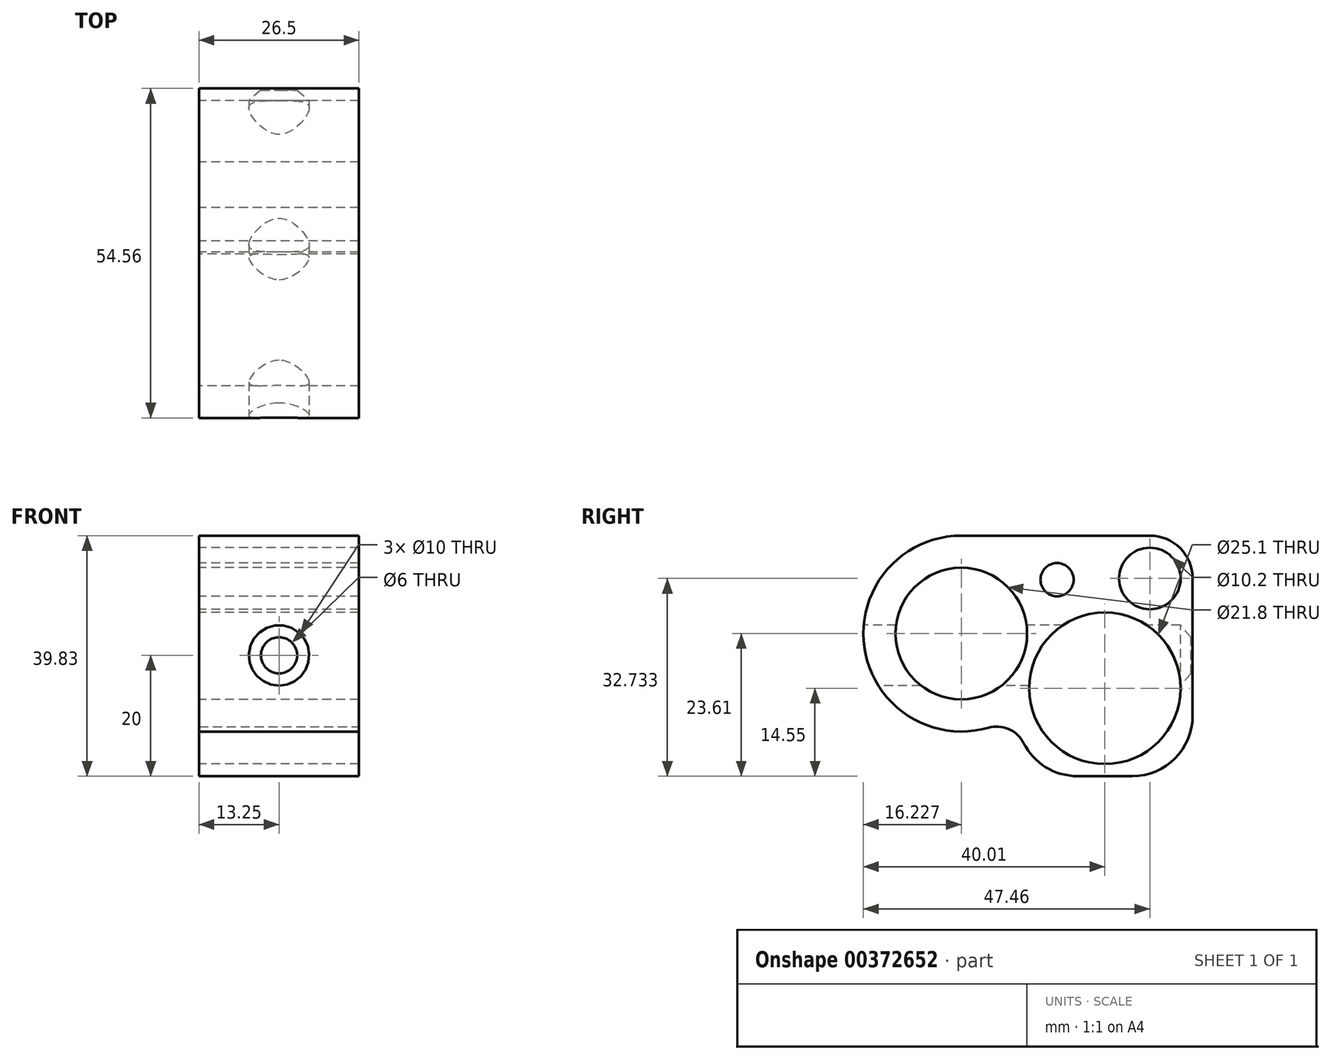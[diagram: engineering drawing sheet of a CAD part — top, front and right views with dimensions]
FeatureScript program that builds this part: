
annotation { "Feature Type Name" : "Feature", "Feature Type Description" : "" }
export const myFeature = defineFeature(function(context is Context, id is Id, definition is map)
    precondition{}
    {
        {
            var Q0;
            Q0=qCreatedBy(makeId("Right.planeOp"),FACE);
            var sketch = newSketch(context, id + "F0", { "sketchPlane" : qUnion([Q0])});
            skCircle(sketch, "E0", {"center": v(0, 0) * mm, "radius": 12.55 * mm});
            skCircle(sketch, "E1", {"center": v(-7.92, 17.98) * mm, "radius": 4.3 * mm, "construction": true});
            skCircle(sketch, "E2", {"center": v(7.45, 18.18) * mm, "radius": 5.1 * mm});
            skLineSegment(sketch, "E3", {"start": v(-7.92, 17.98) * mm, "end": v(0, 0) * mm, "construction": true});
            skLineSegment(sketch, "E4", {"start": v(7.45, 18.18) * mm, "end": v(0, 0) * mm, "construction": true});
            skCircle(sketch, "E5", {"center": v(-23.78, 9.06) * mm, "radius": 10.9 * mm});
            skLineSegment(sketch, "E6", {"start": v(-23.78, 9.06) * mm, "end": v(0, 0) * mm, "construction": true});
            skArc(sketch, "E7", {"start": v(-23.78, 25.28) * mm, "mid": v(-39.27, 4.22) * mm, "end": v(-14.55, -4.28) * mm});
            skArc(sketch, "E8", {"start": v(14.55, 18.18) * mm, "mid": v(12.47, 23.2) * mm, "end": v(7.45, 25.28) * mm});
            skLineSegment(sketch, "E9", {"start": v(7.45, 25.28) * mm, "end": v(-23.78, 25.28) * mm});
            skLineSegment(sketch, "E10", {"start": v(14.55, 18.18) * mm, "end": v(14.55, -14.55) * mm});
            skPoint(sketch, "E10.endSnap0", {"position": v(14.55, 18.18) * mm});
            skLineSegment(sketch, "E11", {"start": v(-14.55, -4.28) * mm, "end": v(-14.55, -14.55) * mm});
            skLineSegment(sketch, "E12", {"start": v(-14.55, -14.55) * mm, "end": v(14.55, -14.55) * mm});
            skCircle(sketch, "E13", {"center": v(-7.92, 17.98) * mm, "radius": 2.75 * mm});
            skSolve(sketch);
        }
        {
            var Q0;
            Q0 = qSketchRegion(id + "F0", true);
            extrude(context, id + "F1", {"entities" : qUnion([Q0]), "depth" : 26.5 * mm, "offsetDistance" : 25 * mm, "symmetric" : true});
        }
        {
            var Q0;
            Q0=makeQuery(id+"F1.opExtrude","SWEPT_EDGE",EDGE,{"disambiguationData":[OSD([sQuery(id+"F0.wireOp",EDGE,"E7"),sQuery(id+"F0.wireOp",EDGE,"E9")])]});
            var Q1;
            Q1=makeQuery(id+"F1.opExtrude","SWEPT_EDGE",EDGE,{"disambiguationData":[OSD([sQuery(id+"F0.wireOp",EDGE,"E8"),sQuery(id+"F0.wireOp",EDGE,"E10")])]});
            var Q2;
            Q2=makeQuery(id+"F1.opExtrude","SWEPT_EDGE",EDGE,{"disambiguationData":[OSD([sQuery(id+"F0.wireOp",EDGE,"E8"),sQuery(id+"F0.wireOp",EDGE,"E9")])]});
            var Q3;
            Q3=makeQuery(id+"F1.opExtrude","SWEPT_EDGE",EDGE,{"disambiguationData":[OSD([sQuery(id+"F0.wireOp",EDGE,"E11"),sQuery(id+"F0.wireOp",EDGE,"E12")])]});
            var Q4;
            Q4=makeQuery(id+"F1.opExtrude","SWEPT_EDGE",EDGE,{"disambiguationData":[OSD([sQuery(id+"F0.wireOp",EDGE,"E10"),sQuery(id+"F0.wireOp",EDGE,"E12")])]});
            fillet(context, id + "F2", {"entities" : qUnion([Q0, Q1, Q2, Q3, Q4]), "radius" : 10 * mm, "tangentPropagation" : true, "allowEdgeOverflow" : false});
        }
        {
            var Q0;
            Q0=makeQuery(id+"F1.opExtrude","SWEPT_EDGE",EDGE,{"disambiguationData":[OSD([sQuery(id+"F0.wireOp",EDGE,"E7"),sQuery(id+"F0.wireOp",EDGE,"E11")])]});
            fillet(context, id + "F3", {"entities" : qUnion([Q0]), "radius" : 5 * mm, "tangentPropagation" : true, "allowEdgeOverflow" : false});
        }
        {
            var Q0;
            Q0=qCreatedBy(makeId("Front.planeOp"),FACE);
            var sketch = newSketch(context, id + "F4", { "sketchPlane" : qUnion([Q0])});
            skCircle(sketch, "E14", {"center": v(0, 5.45) * mm, "radius": 3 * mm});
            skCircle(sketch, "E15", {"center": v(0, 5.45) * mm, "radius": 5 * mm});
            skSolve(sketch);
        }
        {
            var Q0;
            Q0=makeQuery(id+"F4.imprint","IMPRINT",FACE,{"disambiguationData":[TD([[makeQuery(id+"F4.imprint","IMPRINT",EDGE,{"derivedFrom":sQuery(id+"F4.wireOp",EDGE,"E14")}),1.0]])]});
            extrude(context, id + "F5", {"entities" : qUnion([Q0]), "operationType" : NewBodyOperationType.REMOVE, "endBound" : BoundingType.THROUGH_ALL, "oppositeDirection" : true, "depth" : 25 * mm, "offsetDistance" : 25 * mm, "hasSecondDirection" : true, "secondDirectionBound" : BoundingType.THROUGH_ALL, "secondDirectionOppositeDirection" : false, "secondDirectionDepth" : 25 * mm});
        }
        {
            var Q0;
            Q0=makeQuery(id+"F4.imprint","IMPRINT",FACE,{"disambiguationData":[TD([[makeQuery(id+"F4.imprint","IMPRINT",EDGE,{"derivedFrom":sQuery(id+"F4.wireOp",EDGE,"E14")}),-1.0]])]});
            extrude(context, id + "F6", {"entities" : qUnion([Q0]), "operationType" : NewBodyOperationType.REMOVE, "oppositeDirection" : true, "depth" : 12.5 * mm, "offsetDistance" : 25 * mm, "hasSecondDirection" : true, "secondDirectionBound" : BoundingType.THROUGH_ALL, "secondDirectionOppositeDirection" : false, "secondDirectionDepth" : 25 * mm});
        }
        {
            var Q0;
            Q0=qCreatedBy(makeId("Right.planeOp"),FACE);
            var sketch = newSketch(context, id + "F7", { "sketchPlane" : qUnion([Q0])});
            skLineSegment(sketch, "E16", {"start": v(0, 5.45) * mm, "end": v(14.55, 5.45) * mm, "construction": true});
            skLineSegment(sketch, "E17", {"start": v(14.55, 8.45) * mm, "end": v(14.25, 8.45) * mm});
            skLineSegment(sketch, "E18", {"start": v(14.25, 8.45) * mm, "end": v(12.55, 10.45) * mm});
            skLineSegment(sketch, "E19", {"start": v(11.55, 5.45) * mm, "end": v(14.55, 5.45) * mm});
            skLineSegment(sketch, "E20", {"start": v(14.55, 5.45) * mm, "end": v(14.55, 8.45) * mm});
            skLineSegment(sketch, "E21", {"start": v(12.55, 10.45) * mm, "end": v(11.55, 10.45) * mm});
            skLineSegment(sketch, "E22", {"start": v(11.55, 10.45) * mm, "end": v(11.55, 5.45) * mm});
            skSolve(sketch);
        }
        {
            var Q0;
            Q0 = qSketchRegion(id + "F7", true);
            var Q1;
            Q1=sQuery(id+"F7.wireOp",EDGE,"E16");
            revolve(context, id + "F8", {"operationType" : NewBodyOperationType.REMOVE, "surfaceOperationType" : NewSurfaceOperationType.NEW, "entities" : qUnion([Q0]), "axis" : qUnion([Q1]), "revolveType" : RevolveType.FULL});
        }
    });
